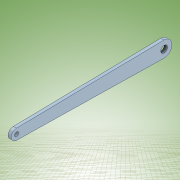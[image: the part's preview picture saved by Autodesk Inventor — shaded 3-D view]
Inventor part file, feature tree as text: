
AUTODESK INVENTOR PART (.ipt)
format: ipt  version: 2022 (Build 260153000, 153)  size: 122,368 bytes
history: native  units: mm
features: other x1, extrude x1, sketch x1
ambient origin geometry x8: Origin, YZ Plane, XZ Plane, XY Plane, X Axis, Y Axis, Z Axis, Center Point
bodies: Body1 (feature_tree)
feature tree (3):
  other  "Sólido1"
  extrude  "Extrusión1"  Depth=10.0mm
  sketch  "Boceto1"  dims[d0=4.0mm d1=10.0mm d2=6.35mm d3=140.0mm d4=15.0mm d5=3.0mm d6=0.0mm]
